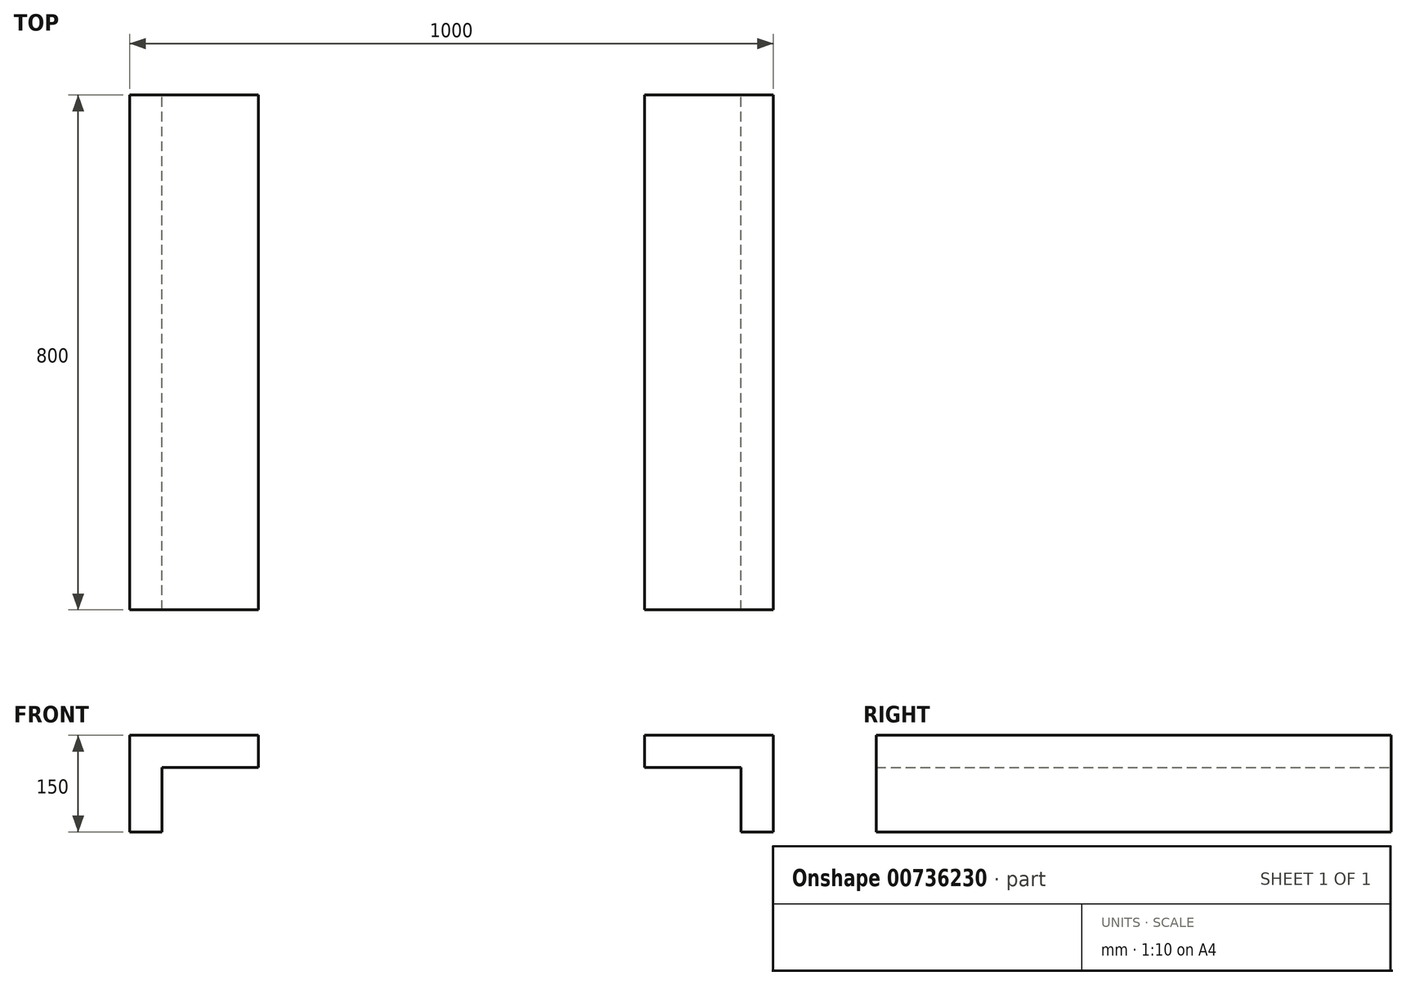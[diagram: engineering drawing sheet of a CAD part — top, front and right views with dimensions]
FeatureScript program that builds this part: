
annotation { "Feature Type Name" : "Feature", "Feature Type Description" : "" }
export const myFeature = defineFeature(function(context is Context, id is Id, definition is map)
    precondition{}
    {
        {
            var Q0;
            Q0=qCreatedBy(makeId("Front.planeOp"),FACE);
            var sketch = newSketch(context, id + "F0", { "sketchPlane" : qUnion([Q0])});
            skLineSegment(sketch, "E0", {"start": v(0, 0) * mm, "end": v(0, 150) * mm});
            skLineSegment(sketch, "E1", {"start": v(0, 150) * mm, "end": v(200, 150) * mm});
            skLineSegment(sketch, "E2", {"start": v(200, 150) * mm, "end": v(200, 100) * mm});
            skLineSegment(sketch, "E3", {"start": v(200, 100) * mm, "end": v(50, 100) * mm});
            skLineSegment(sketch, "E4", {"start": v(50, 100) * mm, "end": v(50, 0) * mm});
            skLineSegment(sketch, "E5", {"start": v(50, 0) * mm, "end": v(0, 0) * mm});
            skSolve(sketch);
        }
        {
            var Q0;
            Q0 = qSketchRegion(id + "F0", true);
            extrude(context, id + "F1", {"entities" : qUnion([Q0]), "depth" : 800 * mm, "offsetDistance" : 25 * mm});
        }
        {
            var Q0;
            Q0=makeQuery(id+"F1.opExtrude","SWEPT_FACE",FACE,{"disambiguationData":[OSD([sQuery(id+"F0.wireOp",EDGE,"E2")])]});
            cPlane(context, id + "F2", {"entities" : qUnion([Q0]), "cplaneType" : CPlaneType.OFFSET, "offset" : 300 * mm, "width" : 150 * mm, "height" : 150 * mm});
        }
        {
            var Q0;
            Q0=makeQuery(id+"F1.opExtrude","SWEPT_BODY",BODY,{"disambiguationData":[OSD([sQuery(id+"F0.wireOp",EDGE,"E0"),sQuery(id+"F0.wireOp",EDGE,"E1"),sQuery(id+"F0.wireOp",EDGE,"E2"),sQuery(id+"F0.wireOp",EDGE,"E3"),sQuery(id+"F0.wireOp",EDGE,"E4"),sQuery(id+"F0.wireOp",EDGE,"E5")])]});
            var Q1;
            Q1=qCreatedBy(id+"F2.planeOp",FACE);
            mirror(context, id + "F3", {"entities" : qUnion([Q0]), "mirrorPlane" : qUnion([Q1])});
        }
    });
